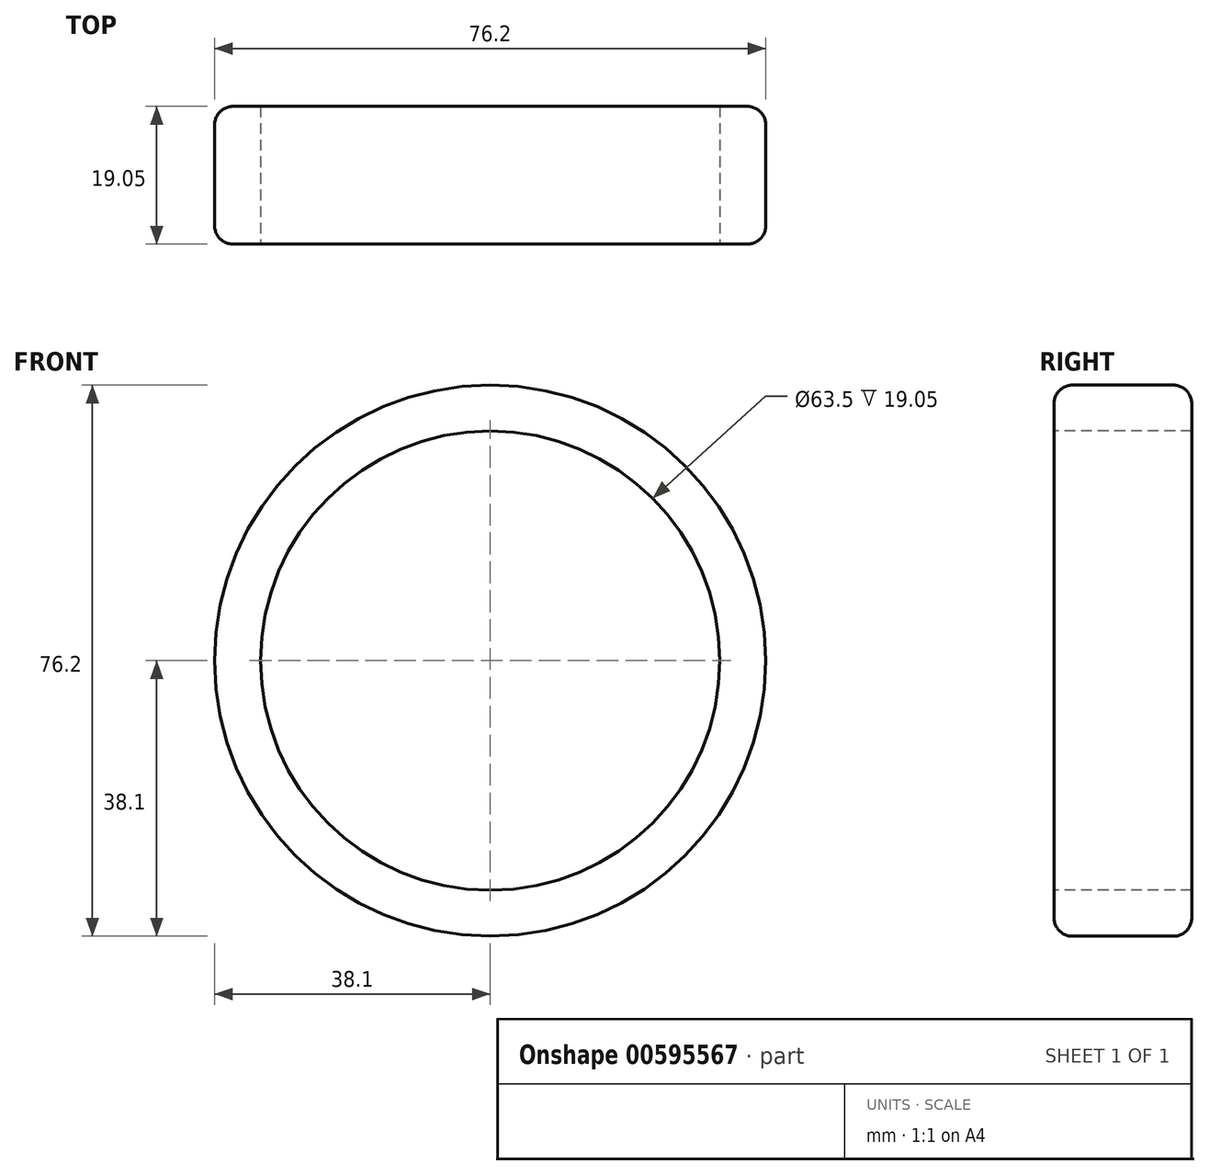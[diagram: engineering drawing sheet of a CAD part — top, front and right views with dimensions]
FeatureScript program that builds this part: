
annotation { "Feature Type Name" : "Feature", "Feature Type Description" : "" }
export const myFeature = defineFeature(function(context is Context, id is Id, definition is map)
    precondition{}
    {
        {
            var Q0;
            Q0=qCreatedBy(makeId("Front.planeOp"),FACE);
            var sketch = newSketch(context, id + "F0", { "sketchPlane" : qUnion([Q0])});
            skCircle(sketch, "E0", {"center": v(0, 0) * mm, "radius": 38.1 * mm});
            skSolve(sketch);
        }
        {
            var Q0;
            Q0=makeQuery(id+"F0.imprint","IMPRINT",FACE,{"disambiguationData":[TD([[makeQuery(id+"F0.imprint","IMPRINT",EDGE,{"derivedFrom":sQuery(id+"F0.wireOp",EDGE,"E0")}),1.0]])]});
            extrude(context, id + "F1", {"entities" : qUnion([Q0]), "depth" : 19.05 * mm, "offsetDistance" : 25.4 * mm});
        }
        {
            var Q0;
            Q0=makeQuery(id+"F1.opExtrude","CAP_FACE",FACE,{"disambiguationData":[OSD([sQuery(id+"F0.wireOp",EDGE,"E0")])],"isStart":false});
            var sketch = newSketch(context, id + "F2", { "sketchPlane" : qUnion([Q0])});
            skCircle(sketch, "E1", {"center": v(0, 0) * mm, "radius": 31.75 * mm});
            skSolve(sketch);
        }
        {
            var Q0;
            Q0 = qSketchRegion(id + "F2", true);
            extrude(context, id + "F3", {"entities" : qUnion([Q0]), "operationType" : NewBodyOperationType.REMOVE, "endBound" : BoundingType.UP_TO_NEXT, "oppositeDirection" : true, "depth" : 25.4 * mm, "offsetDistance" : 25.4 * mm});
        }
        {
            var Q0;
            Q0=makeQuery(id+"F1.opExtrude","CAP_EDGE",EDGE,{"disambiguationData":[OSD([sQuery(id+"F0.wireOp",EDGE,"E0")])],"isStart":false});
            fillet(context, id + "F4", {"entities" : qUnion([Q0]), "radius" : 2.54 * mm, "tangentPropagation" : true, "allowEdgeOverflow" : false});
        }
        {
            var Q0;
            Q0=makeQuery(id+"F3.boolean.opBoolean","COPY",EDGE,{"derivedFrom":makeQuery(id+"F3.opExtrude","CAP_EDGE",EDGE,{"disambiguationData":[OSD([sQuery(id+"F2.wireOp",EDGE,"E1")])],"isStart":true})});
            var Q1;
            Q1=makeQuery(id+"F1.opExtrude","CAP_EDGE",EDGE,{"disambiguationData":[OSD([sQuery(id+"F0.wireOp",EDGE,"E0")])],"isStart":true});
            var Q2;
            Q2=makeQuery(id+"F3.boolean.opBoolean","COPY",EDGE,{"derivedFrom":makeQuery(id+"F3.opExtrude","CAP_EDGE",EDGE,{"disambiguationData":[OSD([sQuery(id+"F2.wireOp",EDGE,"E1")])],"isStart":false})});
            fillet(context, id + "F5", {"entities" : qUnion([Q0, Q1, Q2]), "radius" : 2.54 * mm, "tangentPropagation" : true, "allowEdgeOverflow" : false});
        }
    });
